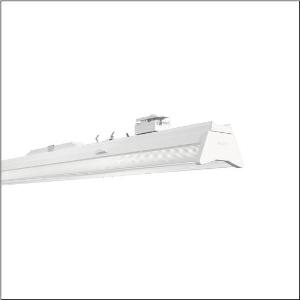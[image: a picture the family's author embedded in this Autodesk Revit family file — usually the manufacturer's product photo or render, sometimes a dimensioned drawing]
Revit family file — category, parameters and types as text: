
# Revit family: licross_r__21_performance_ho_52tm16dn4e5m_a06b
name_source: partatom
category: Lighting Fixtures
units: mm (PartAtom-declared; Revit-internal decimal feet)

## family parameters
Cut with Voids When Loaded = No
Host = Face
Light Source = No
Part Type = Normal
Room Calculation Point = No
Round Connector Dimension = Use Diameter
Shared = No

## types (1)
- --- (1 x LED, 14870 lm, 84.9 W, 4000K)
    Apparent Load = 85 VA
    CIE Flux Codes = 63 87 95 78 100
    Color Rendering = 80
    Color Temperature = 4000K
    Default Elevation = 1800 mm
    Description = Licross® 21 Performance HO, luminaire insert, of sheet steel, galvanised, coil coated, white, length: 1.500mm, width: 120mm, height: 123mm, LED rated luminous flux: 14.870lm, light colour: 840, control gear: DALI 2, with plug, 5-pole, with phase selection, mains connection: 220..240V, AC, 50/60Hz, rated input power: 85W, halogen-free wiring, primary light control with lens, of plastic, primary optical cover: cover, of PMMA, light emission: direct/indirect distribution, primary light characteristic: symmetric, protection rating (complete): IP40, insulation class (complete): insulation class I (protective earthing), certification: CE, ENEC, UKCA, protection symbol: D if used in an environment without relevant dust loads with corresponding accessories, impact resistance: IK06, permissible ambient temperature for indoor applications: -25..+35°C, corresponds to IFS (International Featured Standards) requirements for safety and quality in the food industry, reducing of maximum allowable ambient temperature of 5°C with ceiling mounting, LABS conformity tested according to VDMA 24364:2018-05, packaging unit: 1 piece
    Height = 114 mm
    Lamp = 1 x LED
    Lamp Light Flux = 14870 lm
    Lamp Power = 84.9 W
    Lamp count = 1
    Length = 1500 mm
    Luminous efficacy = 175 lm/W
    Manufacturer = Siteco
    ModVariant = No
    Model = 52TM16DN4E5M
    Mounting Place = Ceiling
    Mounting Type = Pendant
    Number of Poles = 1
    OnlyDefault = Yes
    Power Factor = 1
    Product Name = Licross® 21 Performance HO
    Product group = luminaire insert
    ProductGroupID = 901
    Protection Class = Protection class I
    Protection Degree = IP 40
    RLX_Detail_Level = 1
    RLX_Emergency_Light_Flux = 0 lm
    RLX_Emergency_Type = 0
    RLX_Emergency_Type_DB = No
    RlxData = <blob elided: 33973 chars, md5=1019fae5>
    Socket = socket
    Standby Power = 0 W
    System Light Flux = 14870 lm
    System Power = 85 W
    Type Comments = factory setting: luminous flux: 100 % | dim-lin: 254 | 484 mA
    Type Image = l_1256138.jpg
    URL = http://relux.com
    VarID = @adj_079041
    Voltage = 0 V
    Weight = 0.00 kg
    Width = 120 mm

## geometry (parser evidence)
native form markers: Blend x4, Sweep x12
no freeform markers — native parametric forms only
